# Revit family: Table-LAMMHULTS-COOPER-Table
name_source: partatom
category: Furniture
revit_build: Autodesk Revit 2015 (Build: 20160512_0715(x64)
units: mm (PartAtom-declared; Revit-internal decimal feet)

## types (18) — shared parameters
Assembly Code = E2020
Description = *Please enter mtrl description here for use in mto*
Frame Material = Metal - Chrome - Polished
Keynote = 46.B
Legs Material = Plastic - Black
Manufacturer = LAMMHULTS
Model = COOPER
Table Edge Material = <By Category>
URL = www.lammhults.se

## per-type parameters (varying)
| type | 110x100 | 55x45 | 80x70 | Height | Length | Table Top Height | Table Top Material | Width |
| H45 45x55 Laminate | No | Yes | No | 450 mm  [stored 1.47638 ft] | 450 mm  [stored 1.47638 ft] | 450 mm  [stored 1.47638 ft] | Laminate - High Pressure - White grey | 550 mm |
| H45 45x55 Walnut Veneer | No | Yes | No | 450 mm  [stored 1.47638 ft] | 450 mm  [stored 1.47638 ft] | 450 mm  [stored 1.47638 ft] | Wood - Veneer - Walnut | 550 mm |
| H45 70x80 Laminate | No | No | Yes | 450 mm  [stored 1.47638 ft] | 800 mm  [stored 2.62467 ft] | 450 mm  [stored 1.47638 ft] | Laminate - High Pressure - White grey | 700 mm  [stored 2.29659 ft] |
| H45 70x80 Walnut Veneer | No | No | Yes | 450 mm  [stored 1.47638 ft] | 800 mm  [stored 2.62467 ft] | 450 mm  [stored 1.47638 ft] | Wood - Veneer - Walnut | 700 mm  [stored 2.29659 ft] |
| H45 100x110 Laminate | Yes | No | No | 450 mm  [stored 1.47638 ft] | 1100 mm | 450 mm  [stored 1.47638 ft] | Laminate - High Pressure - White grey | 1000 mm  [stored 3.28084 ft] |
| H45 100x110 Walnut Veneer | Yes | No | No | 450 mm  [stored 1.47638 ft] | 1100 mm | 450 mm  [stored 1.47638 ft] | Wood - Veneer - Walnut | 1000 mm  [stored 3.28084 ft] |
| H52 45x55 Laminate | No | Yes | No | 520 mm  [stored 1.70604 ft] | 450 mm  [stored 1.47638 ft] | 520 mm  [stored 1.70604 ft] | Laminate - High Pressure - White grey | 550 mm |
| H52 45x55 Walnut Veneer | No | Yes | No | 520 mm  [stored 1.70604 ft] | 450 mm  [stored 1.47638 ft] | 520 mm  [stored 1.70604 ft] | Wood - Veneer - Walnut | 550 mm |
| H52 70x80 Laminate | No | No | Yes | 520 mm  [stored 1.70604 ft] | 800 mm  [stored 2.62467 ft] | 520 mm  [stored 1.70604 ft] | Laminate - High Pressure - White grey | 700 mm  [stored 2.29659 ft] |
| H52 70x80 Walnut Veneer | No | No | Yes | 520 mm  [stored 1.70604 ft] | 800 mm  [stored 2.62467 ft] | 520 mm  [stored 1.70604 ft] | Wood - Veneer - Walnut | 700 mm  [stored 2.29659 ft] |
| H52 100x110 Laminate | Yes | No | No | 520 mm  [stored 1.70604 ft] | 1100 mm | 520 mm  [stored 1.70604 ft] | Laminate - High Pressure - White grey | 1000 mm  [stored 3.28084 ft] |
| H52 100x110 Walnut Veneer | Yes | No | No | 520 mm  [stored 1.70604 ft] | 1100 mm | 520 mm  [stored 1.70604 ft] | Wood - Veneer - Walnut | 1000 mm  [stored 3.28084 ft] |
| H72 45x55 Laminate | No | Yes | No | 720 mm  [stored 2.3622 ft] | 450 mm  [stored 1.47638 ft] | 720 mm  [stored 2.3622 ft] | Laminate - High Pressure - White grey | 550 mm |
| H72 45x55 Walnut Veneer | No | Yes | No | 720 mm  [stored 2.3622 ft] | 450 mm  [stored 1.47638 ft] | 720 mm  [stored 2.3622 ft] | Wood - Veneer - Walnut | 550 mm |
| H72 70x80 Laminate | No | No | Yes | 720 mm  [stored 2.3622 ft] | 800 mm  [stored 2.62467 ft] | 720 mm  [stored 2.3622 ft] | Laminate - High Pressure - White grey | 700 mm  [stored 2.29659 ft] |
| H72 70x80 Walnut Veneer | No | No | Yes | 720 mm  [stored 2.3622 ft] | 800 mm  [stored 2.62467 ft] | 720 mm  [stored 2.3622 ft] | Wood - Veneer - Walnut | 700 mm  [stored 2.29659 ft] |
| H72 100x110 Laminate | Yes | No | No | 720 mm  [stored 2.3622 ft] | 1100 mm | 720 mm  [stored 2.3622 ft] | Laminate - High Pressure - White grey | 1000 mm  [stored 3.28084 ft] |
| H72 100x110 Walnut Veneer | Yes | No | No | 720 mm  [stored 2.3622 ft] | 1100 mm | 720 mm  [stored 2.3622 ft] | Wood - Veneer - Walnut | 1000 mm  [stored 3.28084 ft] |

note: [stored X ft] marks values corroborated as IEEE doubles in the binary element streams (Revit-internal decimal feet)

## geometry (parser evidence)
native form markers: Blend x6, Sweep x2
no freeform markers — native parametric forms only
